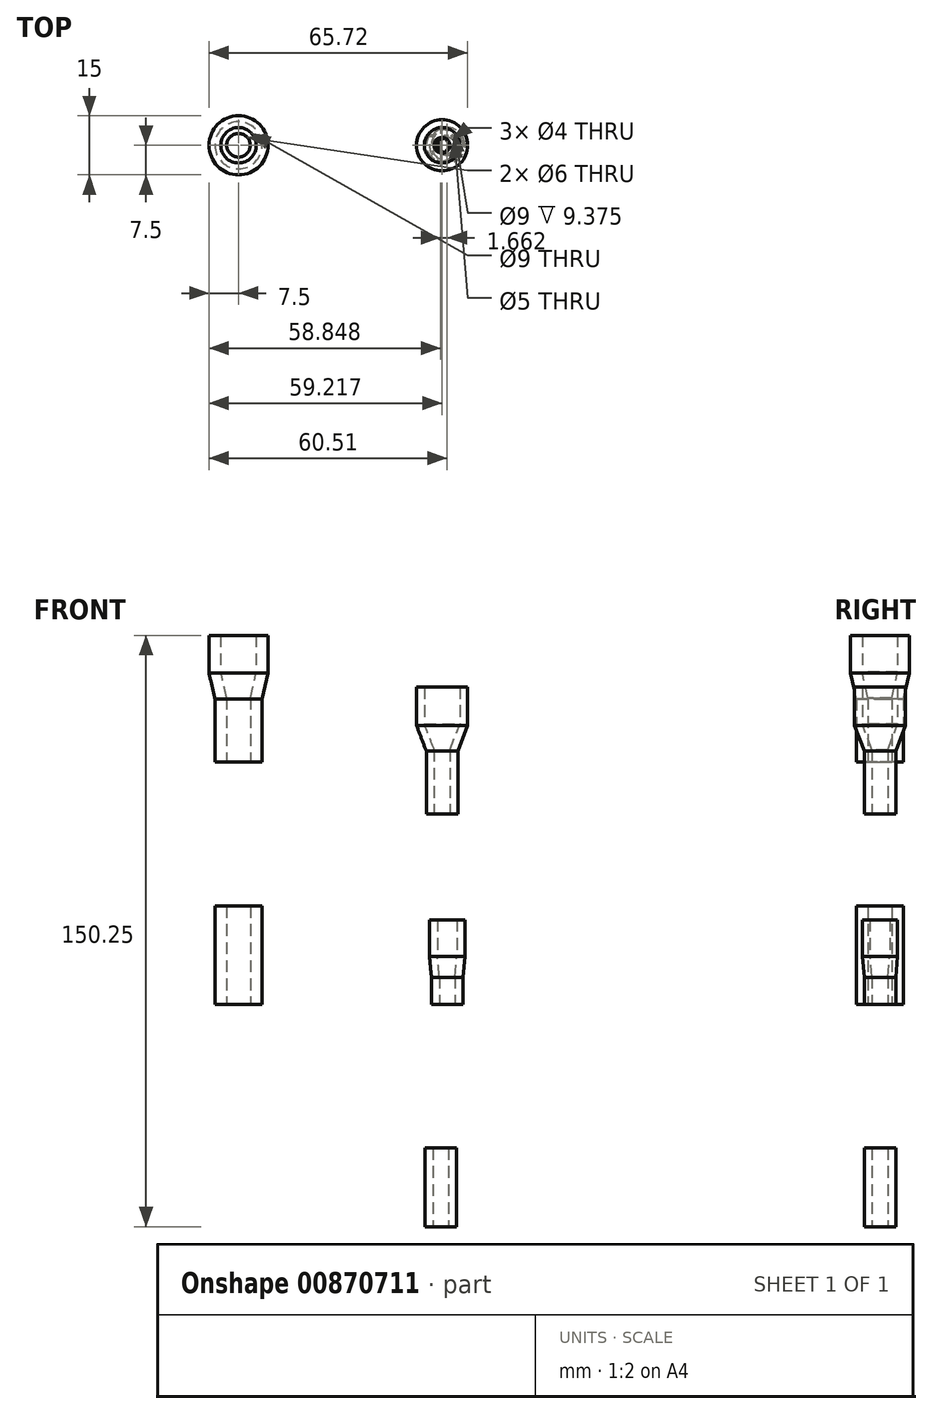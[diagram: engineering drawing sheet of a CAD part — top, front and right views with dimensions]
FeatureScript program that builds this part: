
annotation { "Feature Type Name" : "Feature", "Feature Type Description" : "" }
export const myFeature = defineFeature(function(context is Context, id is Id, definition is map)
    precondition{}
    {
        {
            var Q0;
            Q0=qCreatedBy(makeId("Top.planeOp"),FACE);
            var sketch = newSketch(context, id + "F0", { "sketchPlane" : qUnion([Q0])});
            skCircle(sketch, "E0", {"center": v(0, 0) * mm, "radius": 3 * mm});
            skCircle(sketch, "E1", {"center": v(0, 0) * mm, "radius": 6 * mm});
            skSolve(sketch);
        }
        {
            var Q0;
            Q0 = qSketchRegion(id + "F0", true);
            extrude(context, id + "F1", {"entities" : qUnion([Q0]), "depth" : 25 * mm, "offsetDistance" : 25 * mm});
        }
        {
            var Q0;
            Q0=qCreatedBy(makeId("Front.planeOp"),FACE);
            var sketch = newSketch(context, id + "F2", { "sketchPlane" : qUnion([Q0])});
            skLineSegment(sketch, "E2", {"start": v(0, 61.57) * mm, "end": v(0, 96.03) * mm, "construction": true});
            skLineSegment(sketch, "E3", {"start": v(3, 61.57) * mm, "end": v(6, 61.57) * mm});
            skLineSegment(sketch, "E4", {"start": v(6, 61.57) * mm, "end": v(6, 77.66) * mm});
            skLineSegment(sketch, "E5", {"start": v(6, 77.66) * mm, "end": v(7.5, 84.2) * mm});
            skLineSegment(sketch, "E6", {"start": v(7.5, 84.2) * mm, "end": v(7.5, 93.79) * mm});
            skLineSegment(sketch, "E7", {"start": v(7.5, 93.79) * mm, "end": v(4.5, 93.79) * mm});
            skLineSegment(sketch, "E8", {"start": v(4.5, 93.79) * mm, "end": v(4.5, 84.41) * mm});
            skLineSegment(sketch, "E9", {"start": v(3, 61.57) * mm, "end": v(3, 77.88) * mm});
            skLineSegment(sketch, "E10", {"start": v(3, 77.88) * mm, "end": v(4.5, 84.41) * mm});
            skLineSegment(sketch, "E11.MirrorCS", {"start": v(-3, 61.57) * mm, "end": v(-3, 77.88) * mm});
            skLineSegment(sketch, "E12.MirrorCS", {"start": v(-6, 61.57) * mm, "end": v(-6, 77.66) * mm});
            skLineSegment(sketch, "E13.MirrorCS", {"start": v(-6, 77.66) * mm, "end": v(-7.5, 84.2) * mm});
            skLineSegment(sketch, "E14.MirrorCS", {"start": v(-3, 77.88) * mm, "end": v(-4.5, 84.41) * mm});
            skLineSegment(sketch, "E15.MirrorCS", {"start": v(-3, 61.57) * mm, "end": v(-6, 61.57) * mm});
            skLineSegment(sketch, "E16.MirrorCS", {"start": v(-4.5, 93.79) * mm, "end": v(-4.5, 84.41) * mm});
            skLineSegment(sketch, "E17.MirrorCS", {"start": v(-7.5, 84.2) * mm, "end": v(-7.5, 93.79) * mm});
            skLineSegment(sketch, "E18.MirrorCS", {"start": v(-7.5, 93.79) * mm, "end": v(-4.5, 93.79) * mm});
            skSolve(sketch);
        }
        {
            var Q0;
            Q0=makeQuery(id+"F2.imprint","IMPRINT",FACE,{"disambiguationData":[TD([[makeQuery(id+"F2.imprint","IMPRINT",EDGE,{"derivedFrom":sQuery(id+"F2.wireOp",EDGE,"E3")}),1.0]])]});
            var Q1;
            Q1=sQuery(id+"F2.wireOp",EDGE,"E2");
            revolve(context, id + "F3", {"surfaceOperationType" : NewSurfaceOperationType.NEW, "entities" : qUnion([Q0]), "axis" : qUnion([Q1]), "revolveType" : RevolveType.FULL});
        }
        {
            var Q0;
            Q0=qCreatedBy(makeId("Front.planeOp"),FACE);
            var sketch = newSketch(context, id + "F4", { "sketchPlane" : qUnion([Q0])});
            skLineSegment(sketch, "E19", {"start": v(51.72, 48.4) * mm, "end": v(51.72, 82.86) * mm, "construction": true});
            skLineSegment(sketch, "E20", {"start": v(53.72, 48.4) * mm, "end": v(55.72, 48.4) * mm});
            skLineSegment(sketch, "E21", {"start": v(55.72, 48.4) * mm, "end": v(55.72, 64.34) * mm});
            skLineSegment(sketch, "E22", {"start": v(55.72, 64.34) * mm, "end": v(58.22, 70.87) * mm});
            skLineSegment(sketch, "E23", {"start": v(58.22, 70.87) * mm, "end": v(58.22, 80.62) * mm});
            skLineSegment(sketch, "E24", {"start": v(58.22, 80.62) * mm, "end": v(56.22, 80.62) * mm});
            skLineSegment(sketch, "E25", {"start": v(56.22, 80.62) * mm, "end": v(56.22, 71.24) * mm});
            skLineSegment(sketch, "E26", {"start": v(53.72, 48.4) * mm, "end": v(53.72, 64.7) * mm});
            skLineSegment(sketch, "E27", {"start": v(53.72, 64.7) * mm, "end": v(56.22, 71.24) * mm});
            skLineSegment(sketch, "E28.MirrorCS", {"start": v(49.72, 48.4) * mm, "end": v(49.72, 64.7) * mm});
            skLineSegment(sketch, "E29.MirrorCS", {"start": v(47.72, 48.4) * mm, "end": v(47.72, 64.34) * mm});
            skLineSegment(sketch, "E30.MirrorCS", {"start": v(47.72, 64.34) * mm, "end": v(45.22, 70.87) * mm});
            skLineSegment(sketch, "E31.MirrorCS", {"start": v(49.72, 64.7) * mm, "end": v(47.22, 71.24) * mm});
            skLineSegment(sketch, "E32.MirrorCS", {"start": v(49.72, 48.4) * mm, "end": v(47.72, 48.4) * mm});
            skLineSegment(sketch, "E33.MirrorCS", {"start": v(47.22, 80.62) * mm, "end": v(47.22, 71.24) * mm});
            skLineSegment(sketch, "E34.MirrorCS", {"start": v(45.22, 70.87) * mm, "end": v(45.22, 80.62) * mm});
            skLineSegment(sketch, "E35.MirrorCS", {"start": v(45.22, 80.62) * mm, "end": v(47.22, 80.62) * mm});
            skSolve(sketch);
        }
        {
            var Q0;
            Q0=makeQuery(id+"F4.imprint","IMPRINT",FACE,{"disambiguationData":[TD([[makeQuery(id+"F4.imprint","IMPRINT",EDGE,{"derivedFrom":sQuery(id+"F4.wireOp",EDGE,"E20")}),1.0]])]});
            var Q1;
            Q1=sQuery(id+"F4.wireOp",EDGE,"E19");
            revolve(context, id + "F5", {"surfaceOperationType" : NewSurfaceOperationType.NEW, "entities" : qUnion([Q0]), "axis" : qUnion([Q1]), "revolveType" : RevolveType.FULL});
        }
        {
            var Q0;
            Q0=qCreatedBy(makeId("Front.planeOp"),FACE);
            var sketch = newSketch(context, id + "F6", { "sketchPlane" : qUnion([Q0])});
            skLineSegment(sketch, "E36", {"start": v(53, 0) * mm, "end": v(53, 34.46) * mm, "construction": true});
            skLineSegment(sketch, "E37", {"start": v(55, 0) * mm, "end": v(57, 0) * mm});
            skLineSegment(sketch, "E38", {"start": v(57, 0) * mm, "end": v(57, 6.92) * mm});
            skLineSegment(sketch, "E39", {"start": v(57, 6.92) * mm, "end": v(57.5, 12.24) * mm});
            skLineSegment(sketch, "E40", {"start": v(57.5, 12.24) * mm, "end": v(57.5, 21.5) * mm});
            skLineSegment(sketch, "E41", {"start": v(57.5, 21.5) * mm, "end": v(55.5, 21.5) * mm});
            skLineSegment(sketch, "E42", {"start": v(55.5, 21.5) * mm, "end": v(55.5, 12.33) * mm});
            skLineSegment(sketch, "E43", {"start": v(55, 0) * mm, "end": v(55, 7.01) * mm});
            skLineSegment(sketch, "E44", {"start": v(55, 7.01) * mm, "end": v(55.5, 12.33) * mm});
            skLineSegment(sketch, "E45.MirrorCS", {"start": v(51, 0) * mm, "end": v(51, 7.01) * mm});
            skLineSegment(sketch, "E46.MirrorCS", {"start": v(49, 0) * mm, "end": v(49, 6.92) * mm});
            skLineSegment(sketch, "E47.MirrorCS", {"start": v(49, 6.92) * mm, "end": v(48.5, 12.24) * mm});
            skLineSegment(sketch, "E48.MirrorCS", {"start": v(51, 7.01) * mm, "end": v(50.5, 12.33) * mm});
            skLineSegment(sketch, "E49.MirrorCS", {"start": v(51, 0) * mm, "end": v(49, 0) * mm});
            skLineSegment(sketch, "E50.MirrorCS", {"start": v(50.5, 21.5) * mm, "end": v(50.5, 12.33) * mm});
            skLineSegment(sketch, "E51.MirrorCS", {"start": v(48.5, 12.24) * mm, "end": v(48.5, 21.5) * mm});
            skLineSegment(sketch, "E52.MirrorCS", {"start": v(48.5, 21.5) * mm, "end": v(50.5, 21.5) * mm});
            skSolve(sketch);
        }
        {
            var Q0;
            Q0=makeQuery(id+"F6.imprint","IMPRINT",FACE,{"disambiguationData":[TD([[makeQuery(id+"F6.imprint","IMPRINT",EDGE,{"derivedFrom":sQuery(id+"F6.wireOp",EDGE,"E37")}),1.0]])]});
            var Q1;
            Q1=sQuery(id+"F6.wireOp",EDGE,"E36");
            revolve(context, id + "F7", {"surfaceOperationType" : NewSurfaceOperationType.NEW, "entities" : qUnion([Q0]), "axis" : qUnion([Q1]), "revolveType" : RevolveType.FULL});
        }
        {
            var Q0;
            Q0=qCreatedBy(makeId("Front.planeOp"),FACE);
            var sketch = newSketch(context, id + "F8", { "sketchPlane" : qUnion([Q0])});
            skLineSegment(sketch, "E53", {"start": v(51.35, -56.46) * mm, "end": v(51.35, -22) * mm, "construction": true});
            skLineSegment(sketch, "E54", {"start": v(53.35, -56.46) * mm, "end": v(55.35, -56.46) * mm});
            skLineSegment(sketch, "E55", {"start": v(55.35, -56.46) * mm, "end": v(55.35, -36.46) * mm});
            skLineSegment(sketch, "E56", {"start": v(53.35, -56.46) * mm, "end": v(53.35, -36.46) * mm});
            skLineSegment(sketch, "E57.MirrorCS", {"start": v(49.35, -56.46) * mm, "end": v(49.35, -36.46) * mm});
            skLineSegment(sketch, "E58.MirrorCS", {"start": v(47.35, -56.46) * mm, "end": v(47.35, -36.46) * mm});
            skLineSegment(sketch, "E59.MirrorCS", {"start": v(49.35, -56.46) * mm, "end": v(47.35, -56.46) * mm});
            skLineSegment(sketch, "E60", {"start": v(47.35, -36.46) * mm, "end": v(49.35, -36.46) * mm});
            skLineSegment(sketch, "E61", {"start": v(55.35, -36.46) * mm, "end": v(53.35, -36.46) * mm});
            skSolve(sketch);
        }
        {
            var Q0;
            Q0=makeQuery(id+"F8.imprint","IMPRINT",FACE,{"disambiguationData":[TD([[makeQuery(id+"F8.imprint","IMPRINT",EDGE,{"derivedFrom":sQuery(id+"F8.wireOp",EDGE,"E54")}),1.0]])]});
            var Q1;
            Q1=sQuery(id+"F8.wireOp",EDGE,"E53");
            revolve(context, id + "F9", {"surfaceOperationType" : NewSurfaceOperationType.NEW, "entities" : qUnion([Q0]), "axis" : qUnion([Q1]), "revolveType" : RevolveType.FULL});
        }
    });
